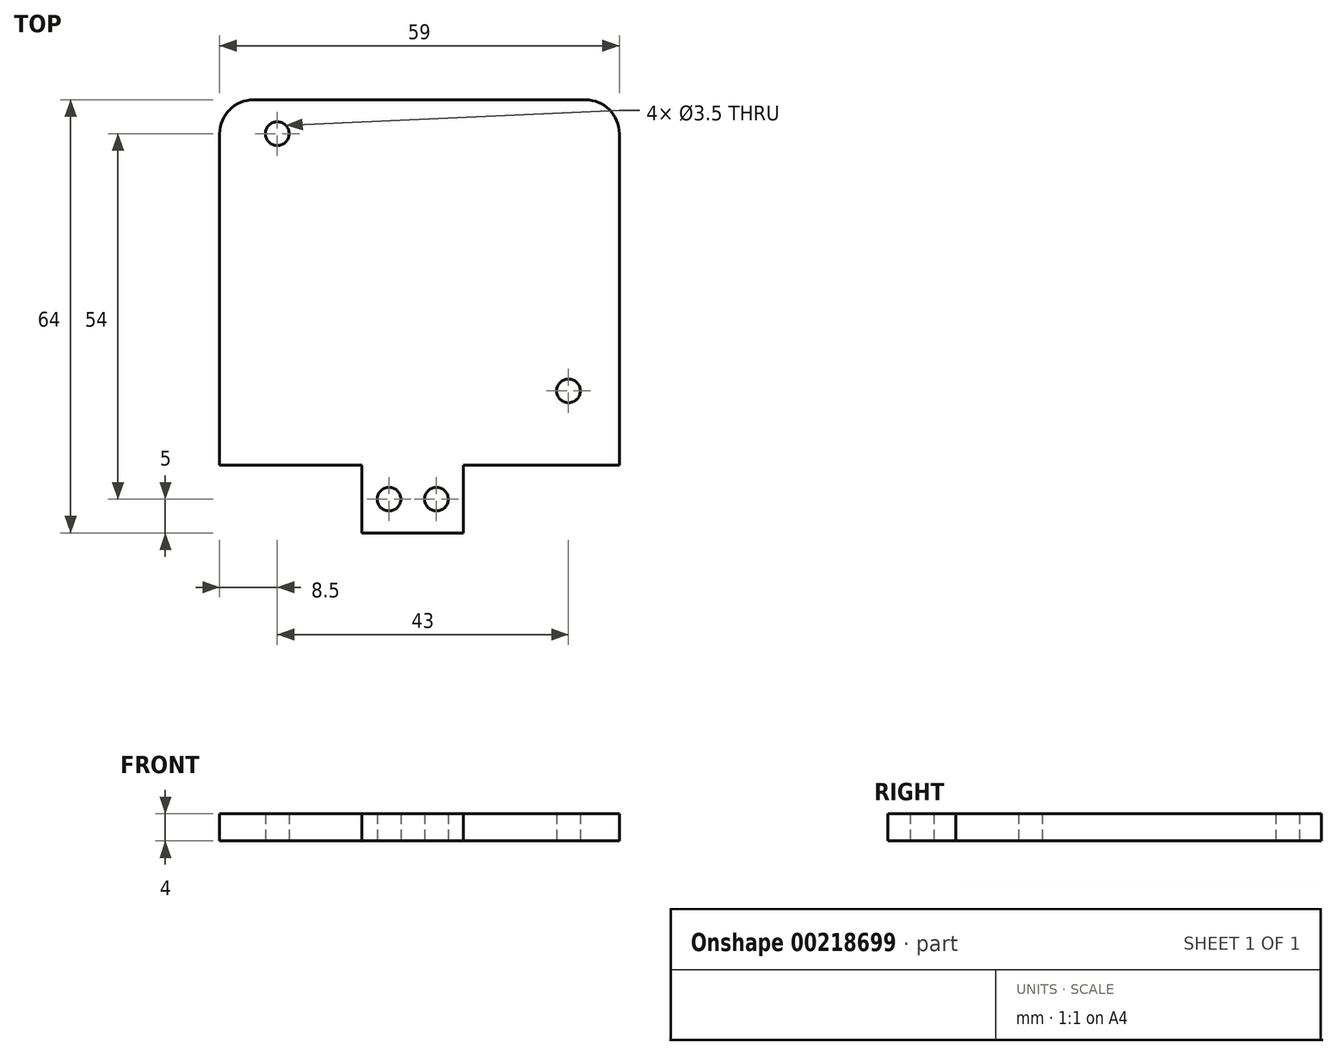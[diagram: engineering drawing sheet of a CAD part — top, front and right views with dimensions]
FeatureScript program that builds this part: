
annotation { "Feature Type Name" : "Feature", "Feature Type Description" : "" }
export const myFeature = defineFeature(function(context is Context, id is Id, definition is map)
    precondition{}
    {
        {
            var Q0;
            Q0=qCreatedBy(makeId("Top.planeOp"),FACE);
            var sketch = newSketch(context, id + "F0", { "sketchPlane" : qUnion([Q0])});
            skLineSegment(sketch, "E0", {"start": v(-36, 54) * mm, "end": v(23, 54) * mm});
            skLineSegment(sketch, "E1", {"start": v(23, 54) * mm, "end": v(23, 0) * mm});
            skLineSegment(sketch, "E2", {"start": v(23, 0) * mm, "end": v(0, 0) * mm});
            skLineSegment(sketch, "E3", {"start": v(0, 0) * mm, "end": v(0, -10) * mm});
            skLineSegment(sketch, "E4", {"start": v(0, -10) * mm, "end": v(-15, -10) * mm});
            skLineSegment(sketch, "E5", {"start": v(-15, -10) * mm, "end": v(-15, 0) * mm});
            skLineSegment(sketch, "E6", {"start": v(-15, 0) * mm, "end": v(-36, 0) * mm});
            skLineSegment(sketch, "E7", {"start": v(-36, 0) * mm, "end": v(-36, 54) * mm});
            skCircle(sketch, "E8", {"center": v(-27.5, 49) * mm, "radius": 1.75 * mm});
            skCircle(sketch, "E9", {"center": v(15.5, 11) * mm, "radius": 1.75 * mm});
            skCircle(sketch, "E10", {"center": v(-11, -5) * mm, "radius": 1.75 * mm});
            skCircle(sketch, "E11", {"center": v(-4, -5) * mm, "radius": 1.75 * mm});
            skSolve(sketch);
        }
        {
            var Q0;
            Q0=makeQuery(id+"F0.imprint","IMPRINT",FACE,{"disambiguationData":[TD([[makeQuery(id+"F0.imprint","IMPRINT",EDGE,{"derivedFrom":sQuery(id+"F0.wireOp",EDGE,"E0")}),-1.0]])]});
            extrude(context, id + "F1", {"entities" : qUnion([Q0]), "depth" : 4 * mm});
        }
        {
            var Q0;
            Q0=makeQuery(id+"F1.opExtrude","SWEPT_EDGE",EDGE,{"disambiguationData":[OSD([sQuery(id+"F0.wireOp",EDGE,"E0"),sQuery(id+"F0.wireOp",EDGE,"E1")])]});
            var Q1;
            Q1=makeQuery(id+"F1.opExtrude","SWEPT_EDGE",EDGE,{"disambiguationData":[OSD([sQuery(id+"F0.wireOp",EDGE,"E0"),sQuery(id+"F0.wireOp",EDGE,"E7")])]});
            fillet(context, id + "F2", {"entities" : qUnion([Q0, Q1]), "radius" : 5 * mm, "tangentPropagation" : true, "allowEdgeOverflow" : false});
        }
    });
